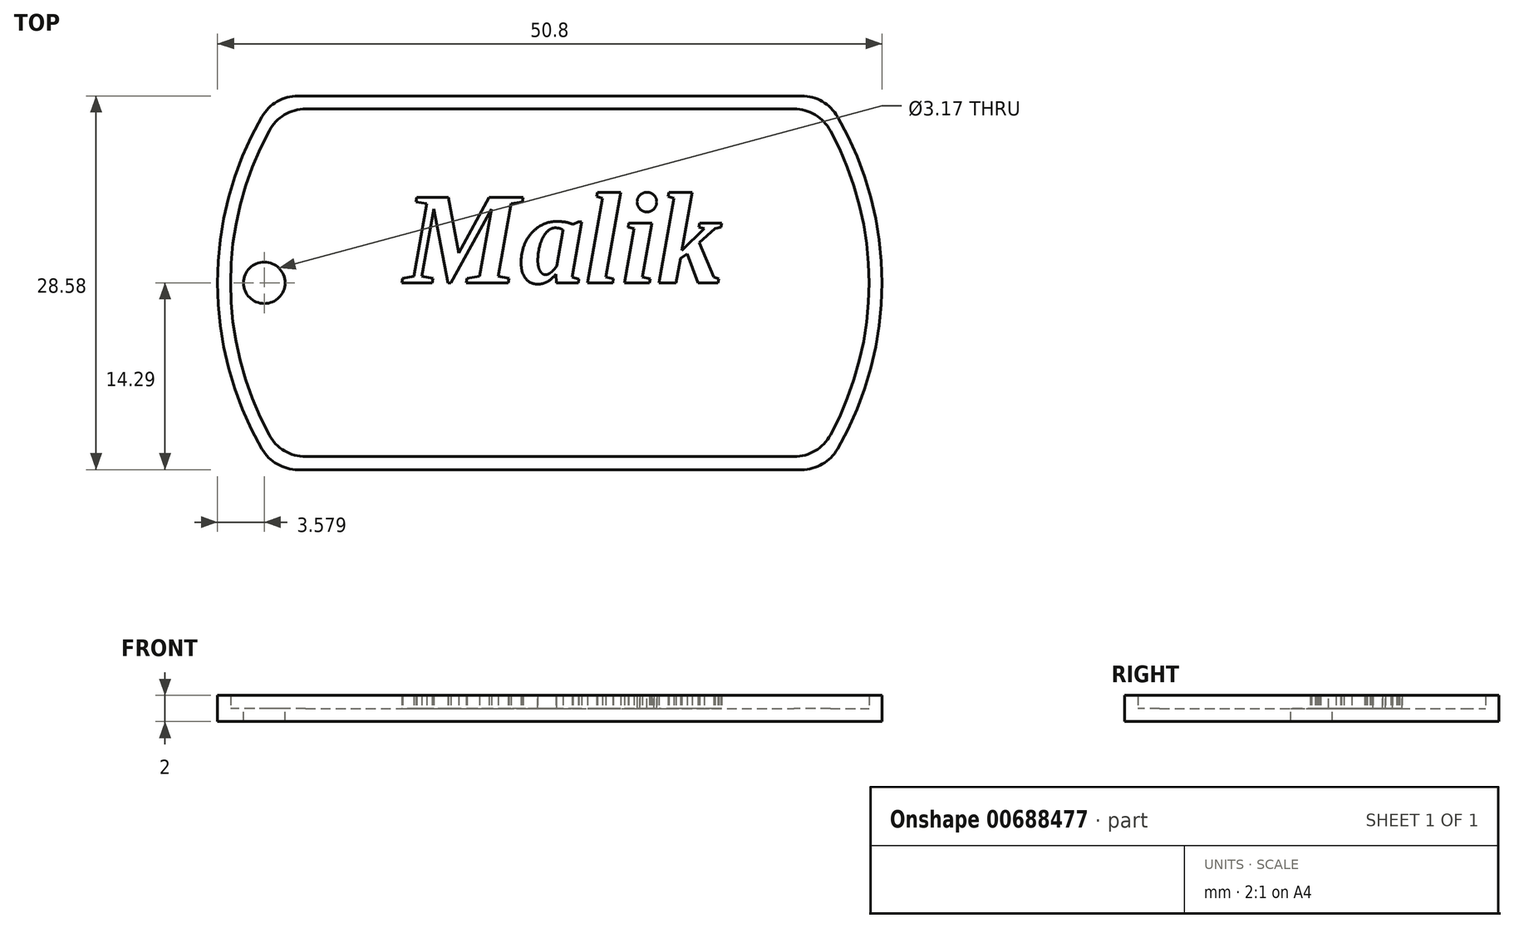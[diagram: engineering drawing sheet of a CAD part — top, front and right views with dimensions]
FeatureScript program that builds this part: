
annotation { "Feature Type Name" : "Feature", "Feature Type Description" : "" }
export const myFeature = defineFeature(function(context is Context, id is Id, definition is map)
    precondition{}
    {
        {
            var Q0;
            Q0=qCreatedBy(makeId("Top.planeOp"),FACE);
            var sketch = newSketch(context, id + "F0", { "sketchPlane" : qUnion([Q0])});
            skArc(sketch, "E0", {"start": v(-22, 12.7) * mm, "mid": v(-25.4, 0) * mm, "end": v(-22, -12.7) * mm});
            skLineSegment(sketch, "E1.top", {"start": v(-19.25, -14.29) * mm, "end": v(19.25, -14.29) * mm});
            skArc(sketch, "E2.trimOffspring", {"start": v(22, -12.7) * mm, "mid": v(25.4, 0) * mm, "end": v(22, 12.7) * mm});
            skLineSegment(sketch, "E3", {"start": v(-19.25, 14.29) * mm, "end": v(19.25, 14.29) * mm});
            skPoint(sketch, "E4.visualSharp", {"position": v(-21, 14.29) * mm});
            skArc(sketch, "E4.filletArc", {"start": v(-19.25, 14.29) * mm, "mid": v(-20.83, 13.86) * mm, "end": v(-22, 12.7) * mm});
            skPoint(sketch, "E5.visualSharp", {"position": v(21, 14.29) * mm});
            skArc(sketch, "E5.filletArc", {"start": v(22, 12.7) * mm, "mid": v(20.83, 13.86) * mm, "end": v(19.25, 14.29) * mm});
            skPoint(sketch, "E6.visualSharp", {"position": v(21, -14.29) * mm});
            skArc(sketch, "E6.filletArc", {"start": v(19.25, -14.29) * mm, "mid": v(20.83, -13.86) * mm, "end": v(22, -12.7) * mm});
            skPoint(sketch, "E7.visualSharp", {"position": v(-21, -14.29) * mm});
            skArc(sketch, "E7.filletArc", {"start": v(-22, -12.7) * mm, "mid": v(-20.83, -13.86) * mm, "end": v(-19.25, -14.29) * mm});
            skSolve(sketch);
        }
        {
            var Q0;
            Q0=makeQuery(id+"F0.imprint","IMPRINT",FACE,{"disambiguationData":[TD([[makeQuery(id+"F0.imprint","IMPRINT",EDGE,{"derivedFrom":sQuery(id+"F0.wireOp",EDGE,"E0")}),1.0]])]});
            extrude(context, id + "F1", {"entities" : qUnion([Q0]), "depth" : 1 * mm, "offsetDistance" : 25.4 * mm});
        }
        {
            var Q0;
            Q0=makeQuery(id+"F1.opExtrude","CAP_FACE",FACE,{"disambiguationData":[OSD([sQuery(id+"F0.wireOp",EDGE,"E0"),sQuery(id+"F0.wireOp",EDGE,"E1.top"),sQuery(id+"F0.wireOp",EDGE,"E2.trimOffspring"),sQuery(id+"F0.wireOp",EDGE,"E3"),sQuery(id+"F0.wireOp",EDGE,"E4.filletArc"),sQuery(id+"F0.wireOp",EDGE,"E5.filletArc"),sQuery(id+"F0.wireOp",EDGE,"E6.filletArc"),sQuery(id+"F0.wireOp",EDGE,"E7.filletArc")])],"isStart":false});
            var sketch = newSketch(context, id + "F2", { "sketchPlane" : qUnion([Q0])});
            skLineSegment(sketch, "E8.0", {"start": v(-18.66, 13.29) * mm, "end": v(18.66, 13.29) * mm});
            skArc(sketch, "E8.1", {"start": v(-21.45, 11.63) * mm, "mid": v(-24.4, 0) * mm, "end": v(-21.45, -11.63) * mm});
            skLineSegment(sketch, "E8.2", {"start": v(-18.66, -13.29) * mm, "end": v(18.66, -13.29) * mm});
            skArc(sketch, "E8.3", {"start": v(21.45, -11.63) * mm, "mid": v(24.4, 0) * mm, "end": v(21.45, 11.63) * mm});
            skPoint(sketch, "E9.visualSharp", {"position": v(-20.46, 13.29) * mm});
            skArc(sketch, "E9.filletArc", {"start": v(-18.66, 13.29) * mm, "mid": v(-20.29, 12.84) * mm, "end": v(-21.45, 11.63) * mm});
            skPoint(sketch, "E10.visualSharp", {"position": v(20.46, 13.29) * mm});
            skArc(sketch, "E10.filletArc", {"start": v(21.45, 11.63) * mm, "mid": v(20.29, 12.84) * mm, "end": v(18.66, 13.29) * mm});
            skPoint(sketch, "E11.visualSharp", {"position": v(20.46, -13.29) * mm});
            skArc(sketch, "E11.filletArc", {"start": v(18.66, -13.29) * mm, "mid": v(20.29, -12.84) * mm, "end": v(21.45, -11.63) * mm});
            skPoint(sketch, "E12.visualSharp", {"position": v(-20.46, -13.29) * mm});
            skArc(sketch, "E12.filletArc", {"start": v(-21.45, -11.63) * mm, "mid": v(-20.29, -12.84) * mm, "end": v(-18.66, -13.29) * mm});
            skLineSegment(sketch, "E13.0", {"start": v(-19.25, 14.29) * mm, "end": v(19.25, 14.29) * mm});
            skArc(sketch, "E13.1", {"start": v(-22, 12.7) * mm, "mid": v(-25.4, 0) * mm, "end": v(-22, -12.7) * mm});
            skLineSegment(sketch, "E13.2", {"start": v(-19.25, -14.29) * mm, "end": v(19.25, -14.29) * mm});
            skArc(sketch, "E13.3", {"start": v(22, -12.7) * mm, "mid": v(25.4, 0) * mm, "end": v(22, 12.7) * mm});
            skPoint(sketch, "E14.visualSharp", {"position": v(-21, -14.29) * mm});
            skArc(sketch, "E14.filletArc", {"start": v(-22, -12.7) * mm, "mid": v(-20.83, -13.86) * mm, "end": v(-19.25, -14.29) * mm});
            skPoint(sketch, "E15.visualSharp", {"position": v(21, -14.29) * mm});
            skArc(sketch, "E15.filletArc", {"start": v(19.25, -14.29) * mm, "mid": v(20.83, -13.86) * mm, "end": v(22, -12.7) * mm});
            skPoint(sketch, "E16.visualSharp", {"position": v(21, 14.29) * mm});
            skArc(sketch, "E16.filletArc", {"start": v(22, 12.7) * mm, "mid": v(20.83, 13.86) * mm, "end": v(19.25, 14.29) * mm});
            skPoint(sketch, "E17.visualSharp", {"position": v(-21, 14.29) * mm});
            skArc(sketch, "E17.filletArc", {"start": v(-19.25, 14.29) * mm, "mid": v(-20.83, 13.86) * mm, "end": v(-22, 12.7) * mm});
            skSolve(sketch);
        }
        {
            var Q0;
            Q0=makeQuery(id+"F2.imprint","IMPRINT",FACE,{"disambiguationData":[TD([[makeQuery(id+"F2.imprint","IMPRINT",EDGE,{"derivedFrom":sQuery(id+"F2.wireOp",EDGE,"E8.0")}),1.0]])]});
            extrude(context, id + "F3", {"entities" : qUnion([Q0]), "operationType" : NewBodyOperationType.ADD, "depth" : 1 * mm, "offsetDistance" : 25.4 * mm});
        }
        {
            var Q0;
            Q0=makeQuery(id+"F1.opExtrude","CAP_FACE",FACE,{"disambiguationData":[OSD([sQuery(id+"F0.wireOp",EDGE,"E0"),sQuery(id+"F0.wireOp",EDGE,"E1.top"),sQuery(id+"F0.wireOp",EDGE,"E2.trimOffspring"),sQuery(id+"F0.wireOp",EDGE,"E3"),sQuery(id+"F0.wireOp",EDGE,"E4.filletArc"),sQuery(id+"F0.wireOp",EDGE,"E5.filletArc"),sQuery(id+"F0.wireOp",EDGE,"E6.filletArc"),sQuery(id+"F0.wireOp",EDGE,"E7.filletArc")])],"isStart":false});
            var sketch = newSketch(context, id + "F4", { "sketchPlane" : qUnion([Q0])});
            skCircle(sketch, "E18", {"center": v(-21.82, 0) * mm, "radius": 1.59 * mm});
            skSolve(sketch);
        }
        {
            var Q0;
            Q0=makeQuery(id+"F4.imprint","IMPRINT",FACE,{"disambiguationData":[TD([[makeQuery(id+"F4.imprint","IMPRINT",EDGE,{"derivedFrom":sQuery(id+"F4.wireOp",EDGE,"E18")}),1.0]])]});
            extrude(context, id + "F5", {"entities" : qUnion([Q0]), "operationType" : NewBodyOperationType.REMOVE, "oppositeDirection" : true, "depth" : 1 * mm, "offsetDistance" : 25.4 * mm});
        }
        {
            var Q0;
            Q0=makeQuery(id+"F2.imprint","IMPRINT",FACE,{"disambiguationData":[TD([[makeQuery(id+"F2.imprint","IMPRINT",EDGE,{"derivedFrom":sQuery(id+"F2.wireOp",EDGE,"E8.0")}),-1.0]])]});
            var sketch = newSketch(context, id + "F6", { "sketchPlane" : qUnion([Q0])});
            skText(sketch, "E19", { "text": "Malik", "fontName": "Tinos-BoldItalic.ttf"});
            const initialGuessF6  = {"E19": [-0.01118, 0, 1, 0, 0.00718]};
            skSetInitialGuess(sketch, initialGuessF6);
            skSolve(sketch);
        }
        {
            var Q0;
            Q0 = qSketchRegion(id + "F6", true);
            extrude(context, id + "F7", {"entities" : qUnion([Q0]), "operationType" : NewBodyOperationType.ADD, "depth" : 1 * mm, "offsetDistance" : 25.4 * mm});
        }
    });
